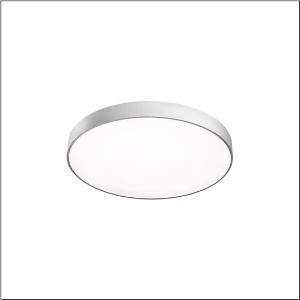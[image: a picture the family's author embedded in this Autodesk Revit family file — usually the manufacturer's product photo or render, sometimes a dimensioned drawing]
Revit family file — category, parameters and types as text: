
# Revit family: round_21_m_51mr36fm8321s
name_source: partatom
category: Lighting Fixtures
units: mm (PartAtom-declared; Revit-internal decimal feet)

## family parameters
Cut with Voids When Loaded = No
Host = Face
Light Source = No
Part Type = Normal
Room Calculation Point = No
Round Connector Dimension = Use Diameter
Shared = No

## types (1)
- --- (1 x LED, 8540 lm, 62.6 W, 3000K)
    Apparent Load = 63 VA
    CIE Flux Codes = 49 80 96 100 100
    Color Rendering = 80
    Color Temperature = 3000K
    Default Elevation = 1800 mm
    Description = Round 21 M, wall and ceiling luminaire, primary optical cover: cover, of PMMA, opal, light emission: direct distribution, primary light characteristic: symmetric, installation type: suspended mounting, surface-mounted, LED, rated luminous flux: 7.700lm, luminous efficacy: 127lm/W, light colour: 830, colour temperature: 3000K, control gear: ON/OFF Multilumen, with terminal, 3-pole, mains connection: 230V, AC, 50/60Hz, rated input power: 61W, housing, of aluminium, coated, silver, diameter: 600mm, height: 62mm, protection rating (complete): IP40, insulation class (complete): insulation class I (protective earthing), certification: CE, impact resistance: IK04, permissible operating ambient temperature: -10..+35°C, packaging unit: 1 piece
    Height = 87 mm
    Lamp = 1 x LED
    Lamp Light Flux = 8540 lm
    Lamp Power = 62.6 W
    Lamp count = 1
    Length = 600 mm
    Luminous efficacy = 136 lm/W
    Manufacturer = Siteco
    ModVariant = No
    Model = 51MR36FM8321S
    Mounting Place = Ceiling
    Mounting Type = Surface mounted
    Number of Poles = 1
    OnlyDefault = Yes
    Power Factor = 1
    Product Name = Round 21 M
    Product group = wall and ceiling luminaire | ceiling mounted
    ProductGroupID = 304
    Protection Class = Protection class I
    Protection Degree = IP 40
    RLX_Detail_Level = 1
    RLX_Emergency_Light_Flux = 0 lm
    RLX_Emergency_Type = 0
    RLX_Emergency_Type_DB = No
    RlxData = <blob elided: 17489 chars, md5=ed80e7dd>
    Socket = socket
    Standby Power = 0 W
    System Light Flux = 8540 lm
    System Power = 63 W
    Type Comments = factory setting: luminous flux: 100 % | (ON | ON | ON | ON) | 700 mA
    Type Image = l_1258303.jpg
    URL = http://relux.com
    VarID = @adj_040947
    Voltage = 0 V
    Weight = 0.00 kg
    Width = 0 mm  [stored 0 ft]

note: [stored X ft] marks values corroborated as IEEE doubles in the binary element streams (Revit-internal decimal feet)

## geometry (parser evidence)
native form markers: Blend x4, Sweep x10
no freeform markers — native parametric forms only
